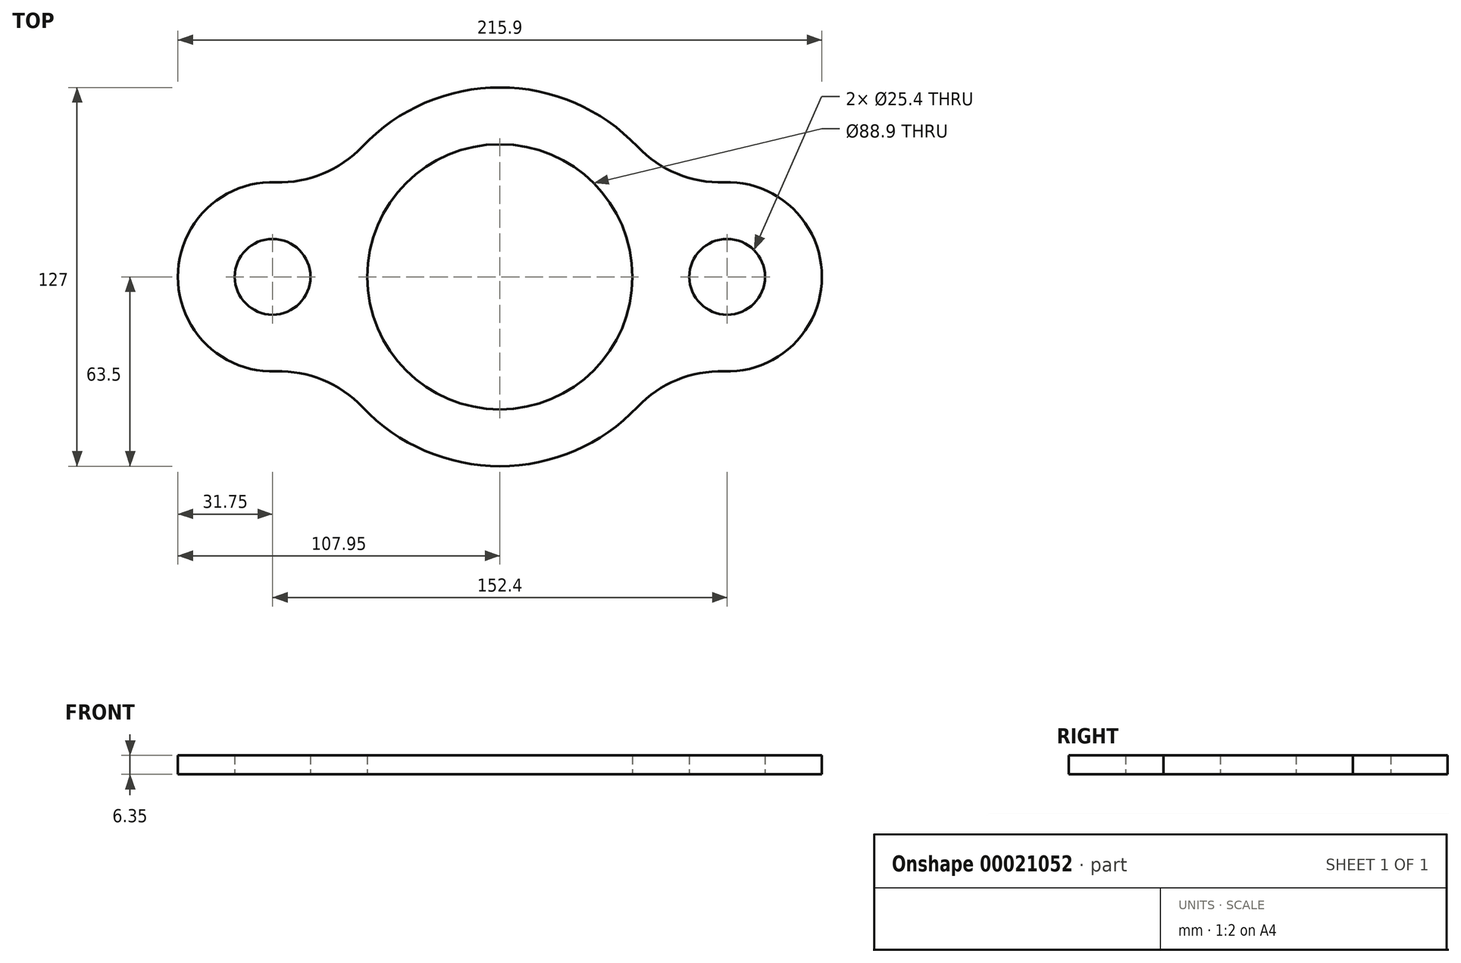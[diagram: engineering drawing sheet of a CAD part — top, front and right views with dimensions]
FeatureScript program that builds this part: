
annotation { "Feature Type Name" : "Feature", "Feature Type Description" : "" }
export const myFeature = defineFeature(function(context is Context, id is Id, definition is map)
    precondition{}
    {
        {
            var Q0;
            Q0=qCreatedBy(makeId("Top.planeOp"),FACE);
            var sketch = newSketch(context, id + "F0", { "sketchPlane" : qUnion([Q0])});
            skLineSegment(sketch, "E0", {"start": v(0, 0) * mm, "end": v(130.2, 0) * mm, "construction": true});
            skLineSegment(sketch, "E1", {"start": v(0, 0) * mm, "end": v(-127.65, 0) * mm, "construction": true});
            skCircle(sketch, "E2", {"center": v(0, 0) * mm, "radius": 44.45 * mm});
            skArc(sketch, "E3", {"start": v(-46.14, -43.63) * mm, "mid": v(0, -63.5) * mm, "end": v(46.14, -43.63) * mm});
            skCircle(sketch, "E4", {"center": v(-76.2, 0) * mm, "radius": 12.7 * mm});
            skCircle(sketch, "E5", {"center": v(76.2, 0) * mm, "radius": 12.7 * mm});
            skArc(sketch, "E6", {"start": v(-75.12, 31.73) * mm, "mid": v(-107.95, 0) * mm, "end": v(-75.12, -31.73) * mm});
            skArc(sketch, "E7", {"start": v(75.12, -31.73) * mm, "mid": v(107.95, 0) * mm, "end": v(75.12, 31.73) * mm});
            skArc(sketch, "E8.trimOffspring", {"start": v(46.14, 43.63) * mm, "mid": v(0, 63.5) * mm, "end": v(-46.14, 43.63) * mm});
            skPoint(sketch, "E9.visualSharp", {"position": v(-57.94, 25.98) * mm});
            skArc(sketch, "E9.filletArc", {"start": v(-75.12, 31.73) * mm, "mid": v(-59.35, 34.56) * mm, "end": v(-46.14, 43.63) * mm});
            skPoint(sketch, "E10.visualSharp", {"position": v(57.94, 25.98) * mm});
            skArc(sketch, "E10.filletArc", {"start": v(46.14, 43.63) * mm, "mid": v(59.35, 34.56) * mm, "end": v(75.12, 31.73) * mm});
            skPoint(sketch, "E11.visualSharp", {"position": v(-57.94, -25.98) * mm});
            skArc(sketch, "E11.filletArc", {"start": v(-46.14, -43.63) * mm, "mid": v(-59.35, -34.56) * mm, "end": v(-75.12, -31.73) * mm});
            skPoint(sketch, "E12.visualSharp", {"position": v(57.94, -25.98) * mm});
            skArc(sketch, "E12.filletArc", {"start": v(75.12, -31.73) * mm, "mid": v(59.35, -34.56) * mm, "end": v(46.14, -43.63) * mm});
            skSolve(sketch);
        }
        {
            var Q0;
            Q0=makeQuery(id+"F0.imprint","IMPRINT",FACE,{"disambiguationData":[TD([[makeQuery(id+"F0.imprint","IMPRINT",EDGE,{"derivedFrom":sQuery(id+"F0.wireOp",EDGE,"E2")}),-1.0]])]});
            extrude(context, id + "F1", {"entities" : qUnion([Q0]), "depth" : 6.35 * mm});
        }
    });
